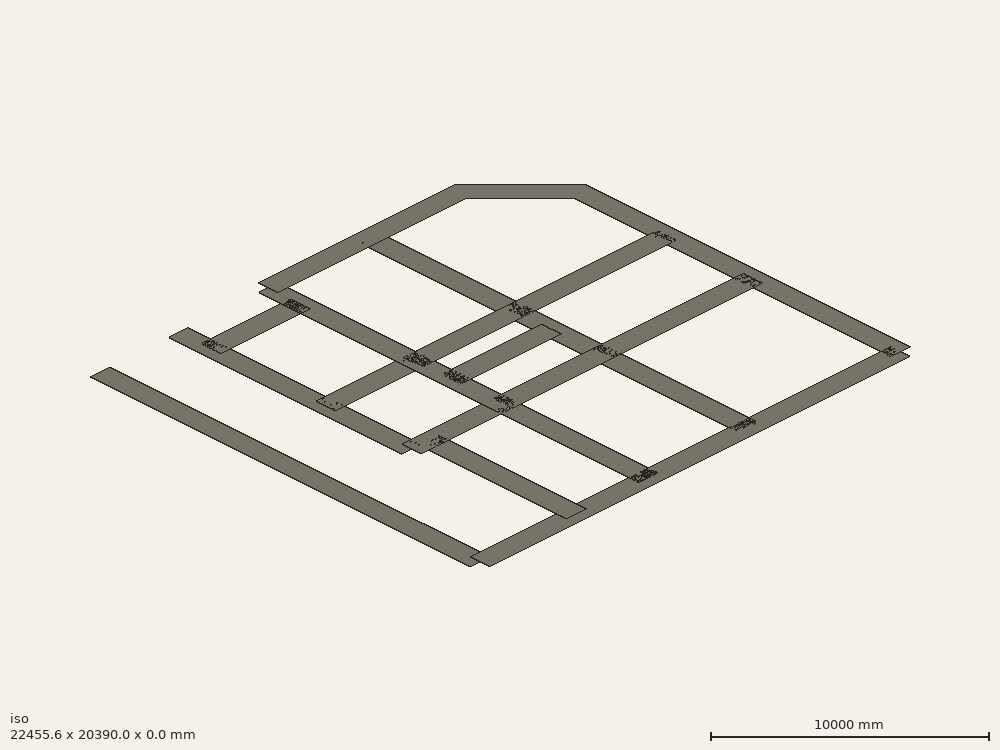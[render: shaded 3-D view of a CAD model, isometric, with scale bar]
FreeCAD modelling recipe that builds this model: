
FCSTD DOCUMENT  (FreeCAD 0.19R24291 (Git))
Label: base_foundation
License: All rights reserved
LicenseURL: http://en.wikipedia.org/wiki/All_rights_reserved
objects: Part::Part2DObjectPython×16, Part::FeaturePython×13
note: 108 computed .brp shape members not serialized (recipe doc carries the construction recipe); baked Part::Feature solids carry a one-line shape summary decoded from their .brp

FEATURE [Part::Part2DObjectPython] Line  # Draft 2D object (typed FeaturePython)
  Area = 0
  ChamferSize = 0
  Closed = false
  End = (8578.07,17740,0)
  FilletRadius = 0
  Length = 4578.18
  MakeFace = true
  Points = (2) [(3999.89,17740,0),(8578.07,17740,0)]
  Start = (3999.89,17740,0)
  Subdivisions = 0
FEATURE [Part::FeaturePython] BaseFoundation012  # Arch/BIM 0 (typed FeaturePython)
  Base = -> Line
  HorizontalArea = 0
  IfcData = attributes={"GlobalId": {"name": "GlobalId", "type": "IfcGloballyUniqueId", "is_enum": false, "enum_values": []}, "Description": {"... (+538 chars omitted),+1 more (map truncated)
  IfcType = 0
  MoveBase = false
  MoveWithHost = false
  PerimeterLength = 0
  PredefinedType = 0
  VerticalArea = 0
  align = 0
  design_type = 0
  fc = 30000
  final_wire_first_point = (0,0,0)
  final_wire_last_point = (0,0,0)
  height = 1100
  ks = 2.4
  layer = 0
  left_width = 500
  main_wire_first_point = (3999.89,17740,0)
  main_wire_last_point = (8578.07,17740,0)
  right_width = 500
  width = 1000
FEATURE [Part::Part2DObjectPython] Line001  # Draft 2D object (typed FeaturePython)
  Area = 0
  ChamferSize = 0
  Closed = false
  End = (21414.7,11895,0)
  FilletRadius = 0
  Length = 17414.9
  MakeFace = true
  Points = (2) [(3999.89,11895,0),(21414.7,11895,0)]
  Start = (3999.89,11895,0)
  Subdivisions = 0
FEATURE [Part::FeaturePython] BaseFoundation014  # Arch/BIM 0 (typed FeaturePython)
  Base = -> Line001
  HorizontalArea = 0
  IfcData = attributes={"GlobalId": {"name": "GlobalId", "type": "IfcGloballyUniqueId", "is_enum": false, "enum_values": []}, "Description": {"... (+538 chars omitted),+1 more (map truncated)
  IfcType = 0
  MoveBase = false
  MoveWithHost = false
  PerimeterLength = 0
  PredefinedType = 0
  VerticalArea = 0
  align = 0
  design_type = 0
  fc = 30000
  final_wire_first_point = (0,0,0)
  final_wire_last_point = (0,0,0)
  height = 1100
  ks = 2.4
  layer = 0
  left_width = 500
  main_wire_first_point = (3999.89,11895,0)
  main_wire_last_point = (21414.7,11895,0)
  right_width = 500
  width = 1000
FEATURE [Part::Part2DObjectPython] Line002  # Draft 2D object (typed FeaturePython)
  Area = 0
  ChamferSize = 0
  Closed = false
  End = (13698.1,10045,0)
  FilletRadius = 0
  Length = 5120
  MakeFace = true
  Points = (2) [(8578.07,10045,0),(13698.1,10045,0)]
  Start = (8578.07,10045,0)
  Subdivisions = 0
FEATURE [Part::FeaturePython] BaseFoundation016  # Arch/BIM 0 (typed FeaturePython)
  Base = -> Line002
  HorizontalArea = 0
  IfcData = attributes={"GlobalId": {"name": "GlobalId", "type": "IfcGloballyUniqueId", "is_enum": false, "enum_values": []}, "Description": {"... (+538 chars omitted),+1 more (map truncated)
  IfcType = 0
  MoveBase = false
  MoveWithHost = false
  PerimeterLength = 0
  PredefinedType = 0
  VerticalArea = 0
  align = 0
  design_type = 0
  fc = 30000
  final_wire_first_point = (0,0,0)
  final_wire_last_point = (0,0,0)
  height = 1100
  ks = 2.4
  layer = 0
  left_width = 500
  main_wire_first_point = (8578.07,10045,0)
  main_wire_last_point = (13698.1,10045,0)
  right_width = 500
  width = 1000
FEATURE [Part::Part2DObjectPython] Line003  # Draft 2D object (typed FeaturePython)
  Area = 0
  ChamferSize = 0
  Closed = false
  End = (21414.7,7499.37,0)
  FilletRadius = 0
  Length = 17414.9
  MakeFace = true
  Points = (2) [(3999.89,7495,0),(21414.7,7499.37,0)]
  Start = (3999.89,7495,0)
  Subdivisions = 0
FEATURE [Part::FeaturePython] BaseFoundation018  # Arch/BIM 0 (typed FeaturePython)
  Base = -> Line003
  HorizontalArea = 0
  IfcData = attributes={"GlobalId": {"name": "GlobalId", "type": "IfcGloballyUniqueId", "is_enum": false, "enum_values": []}, "Description": {"... (+538 chars omitted),+1 more (map truncated)
  IfcType = 0
  MoveBase = false
  MoveWithHost = false
  PerimeterLength = 0
  PredefinedType = 0
  VerticalArea = 0
  align = 0
  design_type = 0
  fc = 30000
  final_wire_first_point = (0,0,0)
  final_wire_last_point = (0,0,0)
  height = 1100
  ks = 2.4
  layer = 0
  left_width = 500
  main_wire_first_point = (3999.89,7495,0)
  main_wire_last_point = (21414.7,7499.37,0)
  right_width = 500
  width = 1000
FEATURE [Part::Part2DObjectPython] Line004  # Draft 2D object (typed FeaturePython)
  Area = 0
  ChamferSize = 0
  Closed = false
  End = (21449.7,0,0)
  FilletRadius = 0
  Length = 21449.7
  MakeFace = true
  Points = (2) [(0,0,0),(21449.7,0,0)]
  Start = (0,0,0)
  Subdivisions = 0
FEATURE [Part::FeaturePython] BaseFoundation020  # Arch/BIM 0 (typed FeaturePython)
  Base = -> Line004
  HorizontalArea = 0
  IfcData = attributes={"GlobalId": {"name": "GlobalId", "type": "IfcGloballyUniqueId", "is_enum": false, "enum_values": []}, "Description": {"... (+538 chars omitted),+1 more (map truncated)
  IfcType = 0
  MoveBase = false
  MoveWithHost = false
  PerimeterLength = 0
  PredefinedType = 0
  VerticalArea = 0
  align = 0
  design_type = 0
  fc = 30000
  final_wire_first_point = (0,0,0)
  final_wire_last_point = (0,0,0)
  height = 1100
  ks = 2.4
  layer = 0
  left_width = 500
  main_wire_first_point = (0,0,0)
  main_wire_last_point = (21449.7,0,0)
  right_width = 500
  width = 1000
FEATURE [Part::Part2DObjectPython] Line005  # Draft 2D object (typed FeaturePython)
  Area = 0
  ChamferSize = 0
  Closed = false
  End = (-5.88239,19377.9,0)
  FilletRadius = 0
  Length = 19377.9
  MakeFace = true
  Points = (2) [(0,0,0),(-5.88239,19377.9,0)]
  Start = (0,0,0)
  Subdivisions = 0
FEATURE [Part::FeaturePython] BaseFoundation022  # Arch/BIM 0 (typed FeaturePython)
  Base = -> Line005
  HorizontalArea = 0
  IfcData = attributes={"GlobalId": {"name": "GlobalId", "type": "IfcGloballyUniqueId", "is_enum": false, "enum_values": []}, "Description": {"... (+538 chars omitted),+1 more (map truncated)
  IfcType = 0
  MoveBase = false
  MoveWithHost = false
  PerimeterLength = 0
  PredefinedType = 0
  VerticalArea = 0
  align = 0
  design_type = 0
  fc = 30000
  final_wire_first_point = (0,0,0)
  final_wire_last_point = (0,0,0)
  height = 1100
  ks = 2.4
  layer = 1
  left_width = 500
  main_wire_first_point = (0,0,0)
  main_wire_last_point = (-5.88239,19377.9,0)
  right_width = 500
  width = 1000
FEATURE [Part::Part2DObjectPython] Line006  # Draft 2D object (typed FeaturePython)
  Area = 0
  ChamferSize = 0
  Closed = false
  End = (3999.89,7495,0)
  FilletRadius = 0
  Length = 11895
  MakeFace = true
  Points = (2) [(3999.89,19390,0),(3999.89,7495,0)]
  Start = (3999.89,19390,0)
  Subdivisions = 0
FEATURE [Part::FeaturePython] BaseFoundation024  # Arch/BIM 0 (typed FeaturePython)
  Base = -> Line006
  HorizontalArea = 0
  IfcData = attributes={"GlobalId": {"name": "GlobalId", "type": "IfcGloballyUniqueId", "is_enum": false, "enum_values": []}, "Description": {"... (+538 chars omitted),+1 more (map truncated)
  IfcType = 0
  MoveBase = false
  MoveWithHost = false
  PerimeterLength = 0
  PredefinedType = 0
  VerticalArea = 0
  align = 0
  design_type = 0
  fc = 30000
  final_wire_first_point = (0,0,0)
  final_wire_last_point = (0,0,0)
  height = 1100
  ks = 2.4
  layer = 1
  left_width = 500
  main_wire_first_point = (3999.89,19390,0)
  main_wire_last_point = (3999.89,7495,0)
  right_width = 500
  width = 1000
FEATURE [Part::Part2DObjectPython] Line007  # Draft 2D object (typed FeaturePython)
  Area = 0
  ChamferSize = 0
  Closed = false
  End = (4899.89,1.48742,0)
  FilletRadius = 0
  Length = 7493.51
  MakeFace = true
  Points = (2) [(4899.89,7495,0),(4899.89,1.48742,0)]
  Start = (4899.89,7495,0)
  Subdivisions = 0
FEATURE [Part::FeaturePython] BaseFoundation026  # Arch/BIM 0 (typed FeaturePython)
  Base = -> Line007
  HorizontalArea = 0
  IfcData = attributes={"GlobalId": {"name": "GlobalId", "type": "IfcGloballyUniqueId", "is_enum": false, "enum_values": []}, "Description": {"... (+538 chars omitted),+1 more (map truncated)
  IfcType = 0
  MoveBase = false
  MoveWithHost = false
  PerimeterLength = 0
  PredefinedType = 0
  VerticalArea = 0
  align = 0
  design_type = 0
  fc = 30000
  final_wire_first_point = (0,0,0)
  final_wire_last_point = (0,0,0)
  height = 1100
  ks = 2.4
  layer = 1
  left_width = 500
  main_wire_first_point = (4899.89,7495,0)
  main_wire_last_point = (4899.89,1.48742,0)
  right_width = 500
  width = 1000
FEATURE [Part::Part2DObjectPython] Line008  # Draft 2D object (typed FeaturePython)
  Area = 0
  ChamferSize = 0
  Closed = false
  End = (8578.07,19390,0)
  FilletRadius = 0
  Length = 19390
  MakeFace = true
  Points = (2) [(8578.07,0,0),(8578.07,19390,0)]
  Start = (8578.07,0,0)
  Subdivisions = 0
FEATURE [Part::FeaturePython] BaseFoundation028  # Arch/BIM 0 (typed FeaturePython)
  Base = -> Line008
  HorizontalArea = 0
  IfcData = attributes={"GlobalId": {"name": "GlobalId", "type": "IfcGloballyUniqueId", "is_enum": false, "enum_values": []}, "Description": {"... (+538 chars omitted),+1 more (map truncated)
  IfcType = 0
  MoveBase = false
  MoveWithHost = false
  PerimeterLength = 0
  PredefinedType = 0
  VerticalArea = 0
  align = 0
  design_type = 0
  fc = 30000
  final_wire_first_point = (0,0,0)
  final_wire_last_point = (0,0,0)
  height = 1100
  ks = 2.4
  layer = 1
  left_width = 500
  main_wire_first_point = (8578.07,0,0)
  main_wire_last_point = (8578.07,19390,0)
  right_width = 500
  width = 1000
FEATURE [Part::Part2DObjectPython] Line009  # Draft 2D object (typed FeaturePython)
  Area = 0
  ChamferSize = 0
  Closed = false
  End = (13698.1,19390,0)
  FilletRadius = 0
  Length = 19390
  MakeFace = true
  Points = (2) [(13698.1,0,0),(13698.1,19390,0)]
  Start = (13698.1,0,0)
  Subdivisions = 0
FEATURE [Part::FeaturePython] BaseFoundation030  # Arch/BIM 0 (typed FeaturePython)
  Base = -> Line009
  HorizontalArea = 0
  IfcData = attributes={"GlobalId": {"name": "GlobalId", "type": "IfcGloballyUniqueId", "is_enum": false, "enum_values": []}, "Description": {"... (+538 chars omitted),+1 more (map truncated)
  IfcType = 0
  MoveBase = false
  MoveWithHost = false
  PerimeterLength = 0
  PredefinedType = 0
  VerticalArea = 0
  align = 0
  design_type = 0
  fc = 30000
  final_wire_first_point = (0,0,0)
  final_wire_last_point = (0,0,0)
  height = 1100
  ks = 2.4
  layer = 1
  left_width = 500
  main_wire_first_point = (13698.1,0,0)
  main_wire_last_point = (13698.1,19390,0)
  right_width = 500
  width = 1000
FEATURE [Part::Part2DObjectPython] Wire  # Draft 2D object (typed FeaturePython)
  Area = 0
  ChamferSize = 0
  Closed = false
  End = (21449.7,0,0)
  FilletRadius = 0
  Length = 30495.6
  MakeFace = true
  Points = (4) [(8578.07,19390,0),(18440.6,19390,0),(21440.5,16391.9,0),(21449.7,0,0)]
  Start = (8578.07,19390,0)
  Subdivisions = 0
FEATURE [Part::FeaturePython] BaseFoundation032  # Arch/BIM 0 (typed FeaturePython)
  Base = -> Wire
  HorizontalArea = 0
  IfcData = attributes={"GlobalId": {"name": "GlobalId", "type": "IfcGloballyUniqueId", "is_enum": false, "enum_values": []}, "Description": {"... (+538 chars omitted),+1 more (map truncated)
  IfcType = 0
  MoveBase = false
  MoveWithHost = false
  PerimeterLength = 0
  PredefinedType = 0
  VerticalArea = 0
  align = 0
  design_type = 0
  fc = 30000
  final_wire_first_point = (0,0,0)
  final_wire_last_point = (0,0,0)
  height = 1100
  ks = 2.4
  layer = 1
  left_width = 500
  main_wire_first_point = (8578.07,19390,0)
  main_wire_last_point = (21449.7,0,0)
  right_width = 500
  width = 1000
FEATURE [Part::Part2DObjectPython] Line010  # Draft 2D object (typed FeaturePython)
  Area = 0
  ChamferSize = 0
  Closed = false
  End = (0,0,0)
  FilletRadius = 0
  Length = 19377.9
  MakeFace = true
  Points = (2) [(-5.88239,19377.9,0),(0,0,0)]
  Start = (-5.88239,19377.9,0)
  Subdivisions = 0
FEATURE [Part::Part2DObjectPython] Wire001  # Draft 2D object (typed FeaturePython)
  Area = 0
  ChamferSize = 0
  Closed = false
  End = (18440.6,19390,0)
  FilletRadius = 0
  Length = 20931.6
  MakeFace = true
  Points = (4) [(-5.88239,19377.9,0),(6178.47,23198.3,0),(12344.8,23715.2,0),(18440.6,19390,0)]
  Start = (-5.88239,19377.9,0)
  Subdivisions = 0
FEATURE [Part::Part2DObjectPython] Wire002  # Draft 2D object (typed FeaturePython)
  Area = 3.48265e+07
  ChamferSize = 0
  Closed = true
  End = (19002,20181.1,0)
  FilletRadius = 0
  Length = 45514
  MakeFace = true
  Points = (8) [(18047.1,18835.4,0),(12154,23016.9,0),(6397.42,22534.3,0),(351.498,18799.4,0),(-515.675,20203.1,0),(5866.14,24145.5,0),(12617,24711.5,0),(19002,20181.1,0)]
  Start = (18047.1,18835.4,0)
  Subdivisions = 0
FEATURE [Part::FeaturePython] RectangularSlab001  # Arch/BIM 77 (typed FeaturePython)
  Auto_Plan = false
  Base = -> Wire001
  HorizontalArea = 0
  IfcData = attributes={"GlobalId": {"name": "GlobalId", "type": "IfcGloballyUniqueId", "is_enum": false, "enum_values": []}, "Description": {"... (+511 chars omitted),+1 more (map truncated)
  IfcType = 77
  MoveBase = false
  MoveWithHost = false
  PerimeterLength = 0
  PredefinedType = 0
  VerticalArea = 0
  align = 1
  design_type = 0
  fc = 30000
  height = 1100
  ks = 2.4
  layer = 0
  left_width = 970
  plan = -> Wire002
  right_width = 680
  width = 1650
FEATURE [Part::Part2DObjectPython] Wire003  # Draft 2D object (typed FeaturePython)
  Area = 0
  ChamferSize = 0
  Closed = false
  End = (21440.5,16391.9,0)
  FilletRadius = 0
  Length = 19625.4
  MakeFace = true
  Points = (4) [(21449.7,0,0),(25054.3,5069.28,0),(25940.5,12417.2,0),(21440.5,16391.9,0)]
  Start = (21449.7,0,0)
  Subdivisions = 0
FEATURE [Part::Part2DObjectPython] Wire004  # Draft 2D object (typed FeaturePython)
  Area = 3.20089e+07
  ChamferSize = 0
  Closed = true
  End = (20798.3,15664.9,0)
  FilletRadius = 0
  Length = 42098.6
  MakeFace = true
  Points = (8) [(21890.6,16901.5,0),(26658.4,12690.4,0),(25708.7,4816.17,0),(22003.9,-394.062,0),(20659.2,562.117,0),(24120.9,5430.35,0),(24916.5,12027.5,0),(20798.3,15664.9,0)]
  Start = (21890.6,16901.5,0)
  Subdivisions = 0
FEATURE [Part::FeaturePython] RectangularSlab002  # Arch/BIM 77 (typed FeaturePython)
  Auto_Plan = false
  Base = -> Wire003
  HorizontalArea = 0
  IfcData = attributes={"GlobalId": {"name": "GlobalId", "type": "IfcGloballyUniqueId", "is_enum": false, "enum_values": []}, "Description": {"... (+511 chars omitted),+1 more (map truncated)
  IfcType = 77
  MoveBase = false
  MoveWithHost = false
  PerimeterLength = 0
  PredefinedType = 0
  VerticalArea = 0
  align = 1
  design_type = 0
  fc = 30000
  height = 1100
  ks = 2.4
  layer = 1
  left_width = 970
  plan = -> Wire004
  right_width = 680
  width = 1650
